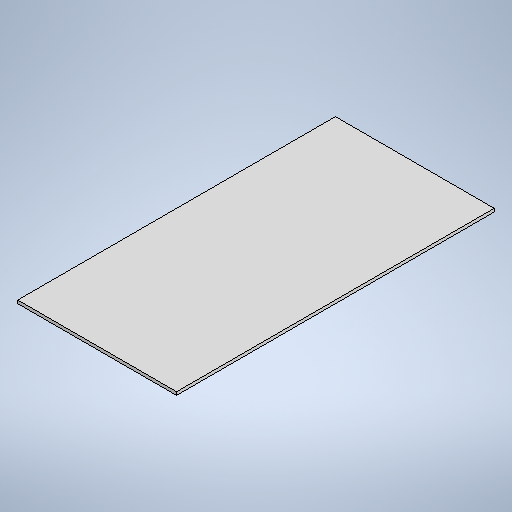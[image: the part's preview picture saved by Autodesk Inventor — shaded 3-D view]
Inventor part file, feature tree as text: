
AUTODESK INVENTOR PART (.ipt)
format: ipt  version: 2025.1 (Build 291241020, 241B)  size: 272,896 bytes
history: native  units: mm
features: other x2, sheet_metal_op x1, sketch x1
ambient origin geometry x8: Origin, YZ Plane, XZ Plane, XY Plane, X Axis, Y Axis, Z Axis, Center Point
bodies: Body1 (feature_tree)
feature tree (4):
  sheet_metal_op  "Face2"
  other  "A-Side Definition"
  sketch  "Sketch1"  dims[d46=2.0mm d61=500.0mm d76=63.281412mm d79=30.0mm d80=48.19529mm d102=80.629223mm d104=53.966969mm d154=100.0mm d155=200.0mm]
  other  "Plate3"
